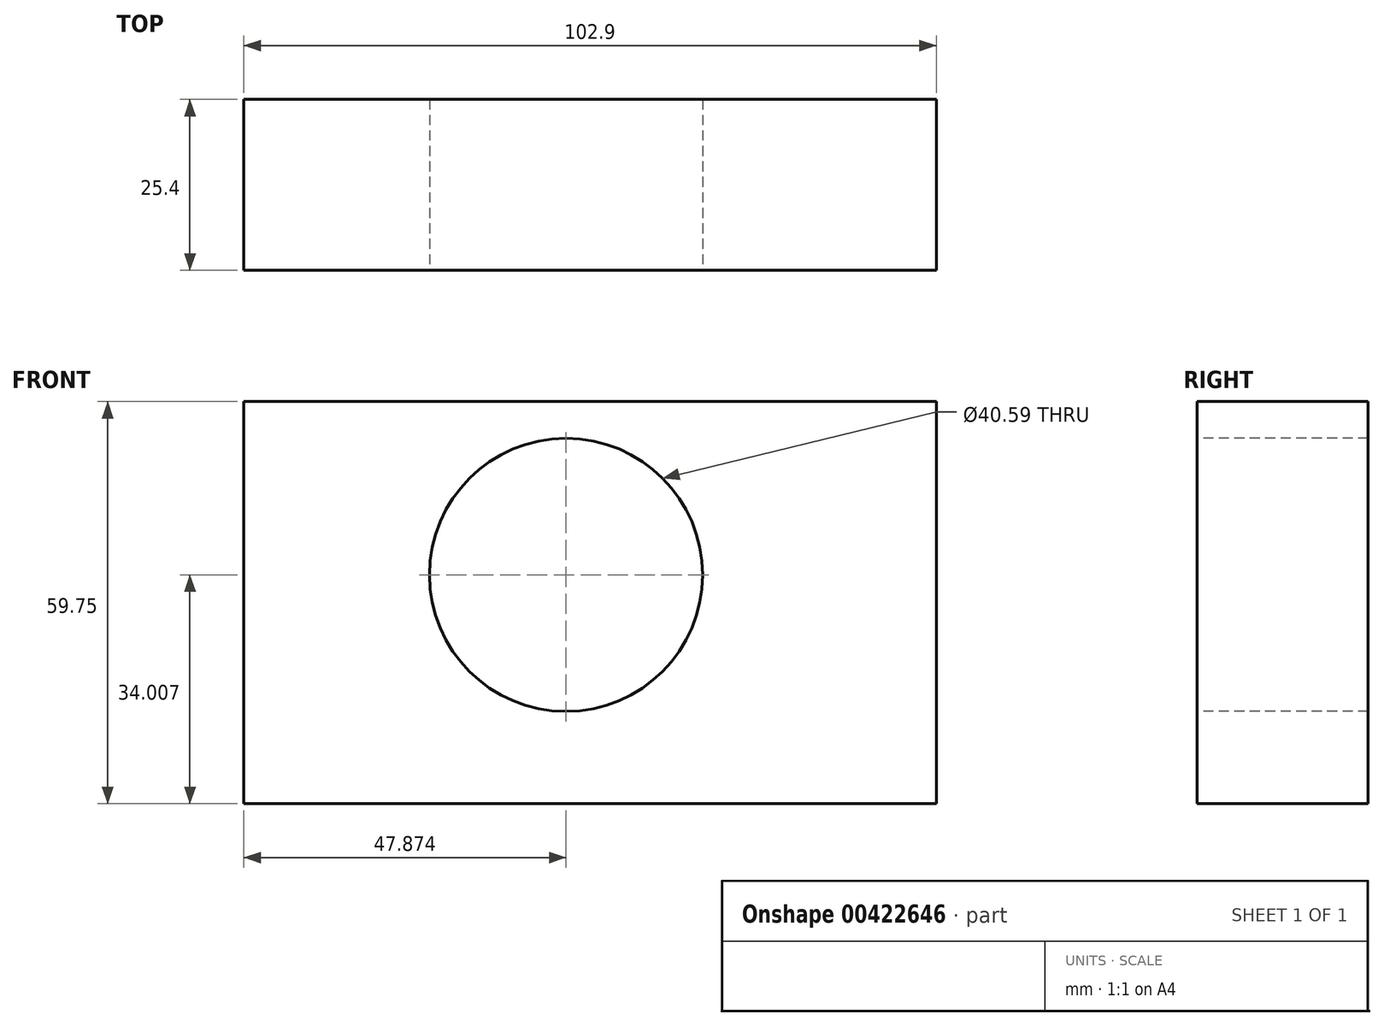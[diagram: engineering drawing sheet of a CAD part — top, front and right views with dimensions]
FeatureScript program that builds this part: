
annotation { "Feature Type Name" : "Feature", "Feature Type Description" : "" }
export const myFeature = defineFeature(function(context is Context, id is Id, definition is map)
    precondition{}
    {
        {
            var Q0;
            Q0=qCreatedBy(makeId("Front.planeOp"),FACE);
            var sketch = newSketch(context, id + "F0", { "sketchPlane" : qUnion([Q0])});
            skLineSegment(sketch, "E0.bottom", {"start": v(-49.58, 30.08) * mm, "end": v(53.32, 30.08) * mm});
            skLineSegment(sketch, "E0.top", {"start": v(-49.58, -29.67) * mm, "end": v(53.32, -29.67) * mm});
            skLineSegment(sketch, "E0.left", {"start": v(-49.58, 30.08) * mm, "end": v(-49.58, -29.67) * mm});
            skLineSegment(sketch, "E0.right", {"start": v(53.32, 30.08) * mm, "end": v(53.32, -29.67) * mm});
            skSolve(sketch);
        }
        {
            var Q0;
            Q0 = qSketchRegion(id + "F0", true);
            extrude(context, id + "F1", {"entities" : qUnion([Q0]), "depth" : 25.4 * mm});
        }
        {
            var Q0;
            Q0=makeQuery(id+"F1.opExtrude","CAP_FACE",FACE,{"disambiguationData":[OSD([sQuery(id+"F0.wireOp",EDGE,"E0.bottom"),sQuery(id+"F0.wireOp",EDGE,"E0.top"),sQuery(id+"F0.wireOp",EDGE,"E0.left"),sQuery(id+"F0.wireOp",EDGE,"E0.right")])],"isStart":false});
            var sketch = newSketch(context, id + "F2", { "sketchPlane" : qUnion([Q0])});
            skCircle(sketch, "E1", {"center": v(-1.7, 4.34) * mm, "radius": 20.3 * mm});
            skPoint(sketch, "E1.first.point", {"position": v(-19.86, 13.4) * mm});
            skPoint(sketch, "E1.second.point", {"position": v(16.16, 13.95) * mm});
            skPoint(sketch, "E1.third.point", {"position": v(9.12, -12.83) * mm});
            skSolve(sketch);
        }
        {
            var Q0;
            Q0 = qSketchRegion(id + "F2", true);
            extrude(context, id + "F3", {"entities" : qUnion([Q0]), "operationType" : NewBodyOperationType.REMOVE, "endBound" : BoundingType.UP_TO_NEXT, "oppositeDirection" : true, "depth" : 25.4 * mm});
        }
    });
